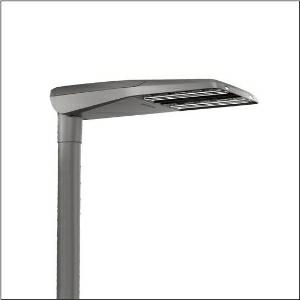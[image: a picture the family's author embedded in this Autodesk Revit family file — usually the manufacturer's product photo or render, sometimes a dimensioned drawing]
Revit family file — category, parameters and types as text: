
# Revit family: streetlight_sl_11_iq_midi___st0_5a_5xc3b41f08me_97ee
name_source: partatom
category: Lighting Fixtures
units: mm (PartAtom-declared; Revit-internal decimal feet)

## family parameters
Cut with Voids When Loaded = No
Host = Face
Light Source = No
Part Type = Normal
Room Calculation Point = No
Round Connector Dimension = Use Diameter
Shared = No

## types (1)
- --- (1 x LED, 18720 lm, 124.7 W, 4000K)
    Apparent Load = 125 VA
    CIE Flux Codes = 43 74 97 100 100
    Color Rendering = 70
    Color Temperature = 4000K
    Default Elevation = 1800 mm
    Description = Streetlight SL 11 iQ midi, mast luminaire, primary light control with 3 zone facetted reflector, of plastic, silver coated, highly specular, primary optical cover: cover, of PMMA, transparent, light distribution: ST0.5a, light emission: direct distribution, primary light characteristic: asymmetric, installation type: post-top, side-entry, LED, High Power LED, rated luminous flux: 18.720lm, luminous efficacy: 150lm/W, light colour: 740, colour temperature: 4000K, control: Street-Remote, optimised constant luminous flux control (CLO 2.0), Desk-Remote (wireless, voltage-free reading and setting of iQ features in the workshop via application-optimized NFC function/RFID function), Light-Fading, Smart-Wire, Night-Set, Lumen-Switch, Temp-Guard, Auto-Match, with cable H07RN-F 5x 1.5mm², mains connection: 220..240V, AC, 50/60Hz, connection cable pre-assembled, cable length: 12,5m, start of lifetime: 125W, end of lifetime: 132W, reduction: 57W, luminaire housing, of diecast aluminium, powder-coated, Siteco® metallic grey (DB 702S), length: 780mm, width: 376mm, height: 118mm, spigot size: 60/76mm (post-top) and 42/60/76mm (side-entry), mast flange for spigot size: 42mm: 5XC10008XM4, 60mm: 5XC10008XM2, 76/60mm: 5XC10108XM1, equipment: Power, protection rating (complete): IP66, insulation class (complete): insulation class II (safety insulation), certification: CE, ENEC, VDE, impact resistance: IK09, permissible operating ambient temperature for outdoor applications: -25..+50°C, standard-compliant lighting for roads and squares, packaging unit: 1 piece

Light Distribution: ST0.5a
    Height = 118 mm
    Lamp = 1 x LED
    Lamp Light Flux = 18720 lm
    Lamp Power = 124.7 W
    Lamp count = 1
    Length = 780 mm
    Luminous efficacy = 150 lm/W
    Manufacturer = Siteco
    ModVariant = No
    Model = 5XC3B41F08ME
    Number of Poles = 1
    OnlyDefault = Yes
    Power Factor = 1
    Product Name = Streetlight SL 11 iQ midi | ST0.5a
    Product group = mast luminaire | pylon top
    ProductGroupID = 6100
    Protection Class = Protection class II
    Protection Degree = IP 66
    RLX_Detail_Level = 1
    RlxData = <blob elided: 75133 chars, md5=2373aa0c>
    Socket = socket
    Standby Power = 0 W
    System Light Flux = 18720 lm
    System Power = 125 W
    Type Comments = factory setting: luminous flux: 100 % | dim-lin: 254 | 557 mA
    Type Image = l_1005960.jpg
    URL = http://relux.com
    VarID = @adj_086745
    Voltage = 0 V
    Weight = 0.00 kg
    Width = 376 mm

## geometry (parser evidence)
native form markers: Blend x4, Sweep x11
no freeform markers — native parametric forms only
